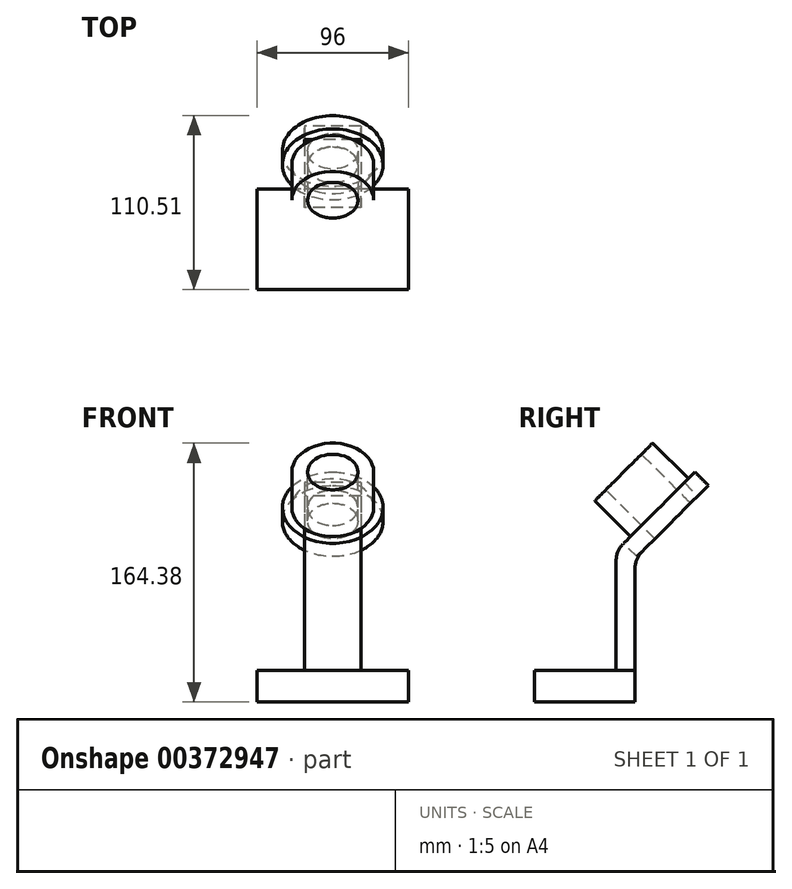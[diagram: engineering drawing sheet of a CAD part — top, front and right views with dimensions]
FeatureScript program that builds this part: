
annotation { "Feature Type Name" : "Feature", "Feature Type Description" : "" }
export const myFeature = defineFeature(function(context is Context, id is Id, definition is map)
    precondition{}
    {
        {
            var Q0;
            Q0=qCreatedBy(makeId("Top.planeOp"),FACE);
            var sketch = newSketch(context, id + "F0", { "sketchPlane" : qUnion([Q0])});
            skLineSegment(sketch, "E0.bottom", {"start": v(48, 32) * mm, "end": v(-48, 32) * mm});
            skLineSegment(sketch, "E0.top", {"start": v(48, -32) * mm, "end": v(-48, -32) * mm});
            skLineSegment(sketch, "E0.left", {"start": v(48, 32) * mm, "end": v(48, -32) * mm});
            skLineSegment(sketch, "E0.right", {"start": v(-48, 32) * mm, "end": v(-48, -32) * mm});
            skPoint(sketch, "E0.middle", {"position": v(0, 0) * mm});
            skSolve(sketch);
        }
        {
            var Q0;
            Q0=makeQuery(id+"F0.imprint","IMPRINT",FACE,{"disambiguationData":[TD([[makeQuery(id+"F0.imprint","IMPRINT",EDGE,{"derivedFrom":sQuery(id+"F0.wireOp",EDGE,"E0.bottom")}),1.0]])]});
            extrude(context, id + "F1", {"entities" : qUnion([Q0]), "depth" : 20 * mm});
        }
        {
            var Q0;
            Q0=qCreatedBy(makeId("Right.planeOp"),FACE);
            var sketch = newSketch(context, id + "F2", { "sketchPlane" : qUnion([Q0])});
            skLineSegment(sketch, "E1", {"start": v(-30.8, 0) * mm, "end": v(32, 0) * mm, "construction": true});
            skLineSegment(sketch, "E2", {"start": v(32, 0) * mm, "end": v(32, 146) * mm, "construction": true});
            skSolve(sketch);
        }
        {
            var Q0;
            Q0=sQuery(id+"F2.wireOp",VERTEX,"E2.end");
            var Q1;
            Q1=qCreatedBy(makeId("Top.planeOp"),FACE);
            cPlane(context, id + "F3", {"entities" : qUnion([Q0, Q1]), "cplaneType" : CPlaneType.PLANE_POINT, "offset" : 25 * mm, "width" : 150 * mm, "height" : 150 * mm});
        }
        {
            var Q0;
            Q0=qCreatedBy(id+"F3.planeOp",FACE);
            var sketch = newSketch(context, id + "F4", { "sketchPlane" : qUnion([Q0])});
            skCircle(sketch, "E3", {"center": v(0, 24.77) * mm, "radius": 26 * mm});
            skLineSegment(sketch, "E4", {"start": v(0, 24.77) * mm, "end": v(-44.36, 24.77) * mm, "construction": true});
            skSolve(sketch);
        }
        {
            var Q0;
            Q0=makeQuery(id+"F4.imprint","IMPRINT",FACE,{"disambiguationData":[TD([[makeQuery(id+"F4.imprint","IMPRINT",EDGE,{"derivedFrom":sQuery(id+"F4.wireOp",EDGE,"E3")}),1.0]])]});
            var Q1;
            Q1=sQuery(id+"F4.wireOp",EDGE,"E3");
            extrude(context, id + "F5", {"entities" : qUnion([Q0]), "surfaceEntities" : qUnion([Q1]), "oppositeDirection" : true, "depth" : 32 * mm});
        }
        {
            var Q0;
            Q0=makeQuery(id+"F5.opExtrude","SWEPT_BODY",BODY,{"disambiguationData":[OSD([sQuery(id+"F4.wireOp",EDGE,"E3")])]});
            var Q1;
            Q1=sQuery(id+"F4.wireOp",EDGE,"E4");
            transform(context, id + "F6", {"entities" : qUnion([Q0]), "transformType" : TransformType.ROTATION, "transformAxis" : qUnion([Q1]), "angle" : 45 * degree, "oppositeDirection" : true, "makeCopy" : false});
        }
        {
            var Q0;
            Q0=makeQuery(id+"F5.opExtrude","CAP_FACE",FACE,{"disambiguationData":[OSD([sQuery(id+"F4.wireOp",EDGE,"E3")])],"isStart":false});
            var sketch = newSketch(context, id + "F7", { "sketchPlane" : qUnion([Q0])});
            skCircle(sketch, "E5", {"center": v(0, 120.75) * mm, "radius": 32 * mm});
            skLineSegment(sketch, "E6", {"start": v(-18, 168.74) * mm, "end": v(-18, 78.24) * mm, "construction": true});
            skSolve(sketch);
        }
        {
            var Q0;
            Q0=qCreatedBy(makeId("Right.planeOp"),FACE);
            var sketch = newSketch(context, id + "F8", { "sketchPlane" : qUnion([Q0])});
            skLineSegment(sketch, "E7", {"start": v(71.75, 130.75) * mm, "end": v(36.4, 95.4) * mm});
            skLineSegment(sketch, "E8", {"start": v(32, 84.79) * mm, "end": v(32, 20) * mm});
            skPoint(sketch, "E9.visualSharp", {"position": v(32, 91) * mm});
            skArc(sketch, "E9.filletArc", {"start": v(36.4, 95.4) * mm, "mid": v(33.14, 90.53) * mm, "end": v(32, 84.79) * mm});
            skLineSegment(sketch, "E10.0", {"start": v(63.26, 139.24) * mm, "end": v(24.4, 100.37) * mm});
            skLineSegment(sketch, "E11.0", {"start": v(20, 89.76) * mm, "end": v(20, 20) * mm});
            skArc(sketch, "E12", {"start": v(24.4, 100.37) * mm, "mid": v(21.14, 95.5) * mm, "end": v(20, 89.76) * mm});
            skLineSegment(sketch, "E13", {"start": v(63.26, 139.24) * mm, "end": v(71.75, 130.75) * mm});
            skLineSegment(sketch, "E14", {"start": v(20, 20) * mm, "end": v(32, 20) * mm});
            skSolve(sketch);
        }
        {
            var Q0;
            Q0=makeQuery(id+"F8.imprint","IMPRINT",FACE,{"disambiguationData":[TD([[makeQuery(id+"F8.imprint","IMPRINT",EDGE,{"derivedFrom":sQuery(id+"F8.wireOp",EDGE,"E7")}),-1.0]])]});
            extrude(context, id + "F9", {"entities" : qUnion([Q0]), "endBound" : BoundingType.SYMMETRIC, "depth" : 36 * mm});
        }
        {
            var Q0;
            Q0=makeQuery(id+"F7.imprint","IMPRINT",FACE,{"disambiguationData":[TD([[makeQuery(id+"F7.imprint","IMPRINT",EDGE,{"derivedFrom":sQuery(id+"F7.wireOp",EDGE,"E5")}),1.0]])]});
            var Q1;
            Q1=makeQuery(id+"F7.imprint","IMPRINT",FACE,{"disambiguationData":[TD([[makeQuery(id+"F7.imprint","IMPRINT",EDGE,{"derivedFrom":makeQuery(id+"F5.opExtrude","CAP_EDGE",EDGE,{"disambiguationData":[OSD([sQuery(id+"F4.wireOp",EDGE,"E3")])],"isStart":false})}),-1.0]])]});
            var Q2;
            Q2=sQuery(id+"F7.wireOp",EDGE,"E5");
            extrude(context, id + "F10", {"entities" : qUnion([Q0, Q1]), "surfaceEntities" : qUnion([Q2]), "depth" : 12 * mm});
        }
        {
            var Q0;
            Q0=makeQuery(id+"F5.opExtrude","CAP_FACE",FACE,{"disambiguationData":[OSD([sQuery(id+"F4.wireOp",EDGE,"E3")])],"isStart":true});
            var sketch = newSketch(context, id + "F11", { "sketchPlane" : qUnion([Q0])});
            skCircle(sketch, "E15", {"center": v(0, 120.75) * mm, "radius": 16 * mm});
            skSolve(sketch);
        }
        {
            var Q0;
            Q0=makeQuery(id+"F11.imprint","IMPRINT",FACE,{"disambiguationData":[TD([[makeQuery(id+"F11.imprint","IMPRINT",EDGE,{"derivedFrom":sQuery(id+"F11.wireOp",EDGE,"E15")}),1.0]])]});
            extrude(context, id + "F12", {"entities" : qUnion([Q0]), "operationType" : NewBodyOperationType.REMOVE, "oppositeDirection" : true, "depth" : 49.1 * mm});
        }
    });
